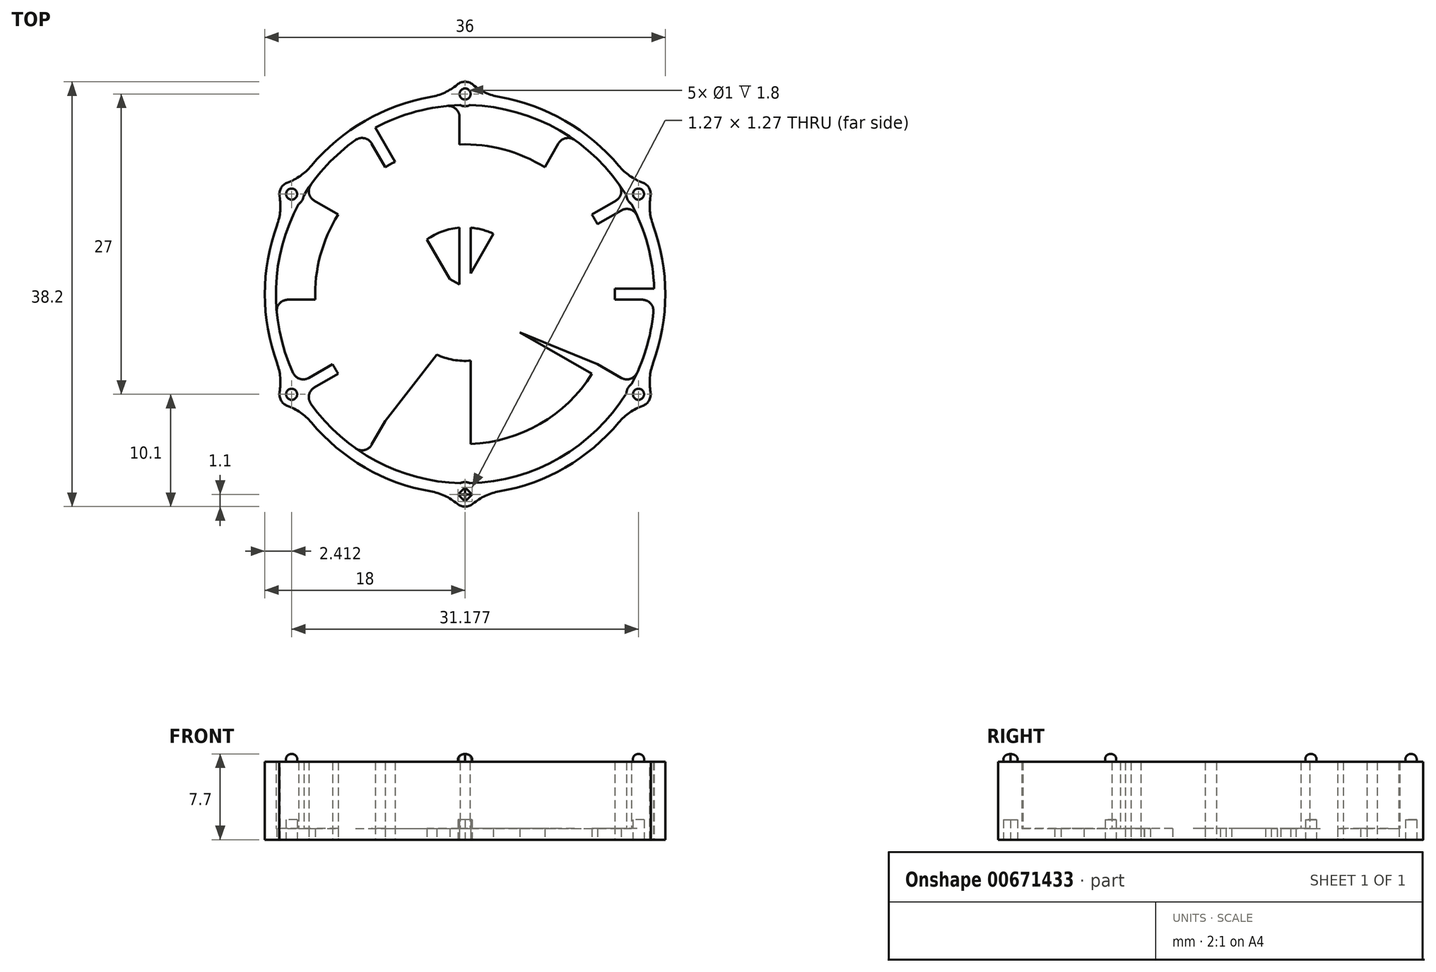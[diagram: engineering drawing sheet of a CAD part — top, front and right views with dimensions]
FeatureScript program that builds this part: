
annotation { "Feature Type Name" : "Feature", "Feature Type Description" : "" }
export const myFeature = defineFeature(function(context is Context, id is Id, definition is map)
    precondition{}
    {
        {
            var Q0;
            Q0=qCreatedBy(makeId("Top.planeOp"),FACE);
            var sketch = newSketch(context, id + "F0", { "sketchPlane" : qUnion([Q0])});
            skCircle(sketch, "E0", {"center": v(0, 0) * mm, "radius": 18 * mm});
            skCircle(sketch, "E1.0", {"center": v(0, 0) * mm, "radius": 17 * mm});
            skLineSegment(sketch, "E2.bottom", {"start": v(8.56, 15.83) * mm, "end": v(9.43, 15.33) * mm});
            skLineSegment(sketch, "E2.top", {"start": v(-9.43, -15.33) * mm, "end": v(-8.56, -15.83) * mm});
            skLineSegment(sketch, "E2.left", {"start": v(8.56, 15.83) * mm, "end": v(-9.43, -15.33) * mm});
            skLineSegment(sketch, "E2.right", {"start": v(9.43, 15.33) * mm, "end": v(-8.56, -15.83) * mm});
            skLineSegment(sketch, "E3.bottom", {"start": v(15.33, 9.43) * mm, "end": v(15.83, 8.56) * mm});
            skLineSegment(sketch, "E3.top", {"start": v(-15.83, -8.56) * mm, "end": v(-15.33, -9.43) * mm});
            skLineSegment(sketch, "E3.left", {"start": v(15.33, 9.43) * mm, "end": v(-15.83, -8.56) * mm});
            skLineSegment(sketch, "E3.right", {"start": v(15.83, 8.56) * mm, "end": v(-15.33, -9.43) * mm});
            skLineSegment(sketch, "E4", {"start": v(-38.35, 0) * mm, "end": v(39.17, 0) * mm, "construction": true});
            skLineSegment(sketch, "E5", {"start": v(0, 42.5) * mm, "end": v(0, -42.47) * mm, "construction": true});
            skLineSegment(sketch, "E6.bottom", {"start": v(-18, 0.5) * mm, "end": v(18, 0.5) * mm});
            skLineSegment(sketch, "E6.top", {"start": v(-18, -0.5) * mm, "end": v(18, -0.5) * mm});
            skLineSegment(sketch, "E6.left", {"start": v(-18, 0.5) * mm, "end": v(-18, -0.5) * mm});
            skLineSegment(sketch, "E6.right", {"start": v(18, 0.5) * mm, "end": v(18, -0.5) * mm});
            skLineSegment(sketch, "E7.bottom", {"start": v(-15.33, 9.43) * mm, "end": v(15.83, -8.56) * mm});
            skLineSegment(sketch, "E7.top", {"start": v(-15.83, 8.56) * mm, "end": v(15.33, -9.43) * mm});
            skLineSegment(sketch, "E7.left", {"start": v(-15.33, 9.43) * mm, "end": v(-15.83, 8.56) * mm});
            skLineSegment(sketch, "E7.right", {"start": v(15.83, -8.56) * mm, "end": v(15.33, -9.43) * mm});
            skLineSegment(sketch, "E8.bottom", {"start": v(-0.5, 18) * mm, "end": v(0.5, 18) * mm});
            skLineSegment(sketch, "E8.top", {"start": v(-0.5, -18) * mm, "end": v(0.5, -18) * mm});
            skLineSegment(sketch, "E8.left", {"start": v(-0.5, 18) * mm, "end": v(-0.5, -18) * mm});
            skLineSegment(sketch, "E8.right", {"start": v(0.5, 18) * mm, "end": v(0.5, -18) * mm});
            skLineSegment(sketch, "E9.bottom", {"start": v(-9.43, 15.33) * mm, "end": v(-8.56, 15.83) * mm});
            skLineSegment(sketch, "E9.top", {"start": v(8.56, -15.83) * mm, "end": v(9.43, -15.33) * mm});
            skLineSegment(sketch, "E9.left", {"start": v(-9.43, 15.33) * mm, "end": v(8.56, -15.83) * mm});
            skLineSegment(sketch, "E9.right", {"start": v(-8.56, 15.83) * mm, "end": v(9.43, -15.33) * mm});
            skCircle(sketch, "E10", {"center": v(0, 0) * mm, "radius": 13.47 * mm});
            skCircle(sketch, "E11", {"center": v(0, 0) * mm, "radius": 6 * mm});
            skLineSegment(sketch, "E12", {"start": v(-7.16, -11.4) * mm, "end": v(-2.56, -5.43) * mm});
            skLineSegment(sketch, "E13", {"start": v(4.93, -3.42) * mm, "end": v(11.9, -6.3) * mm});
            skSolve(sketch);
        }
        {
            var Q0;
            Q0=qCreatedBy(makeId("Top.planeOp"),FACE);
            var sketch = newSketch(context, id + "F1", { "sketchPlane" : qUnion([Q0])});
            skCircle(sketch, "E14", {"center": v(0, 0) * mm, "radius": 18 * mm});
            skCircle(sketch, "E15", {"center": v(0, 0) * mm, "radius": 17 * mm});
            skSolve(sketch);
        }
        {
            var Q0;
            Q0=makeQuery(id+"F1.imprint","IMPRINT",FACE,{"disambiguationData":[TD([[makeQuery(id+"F1.imprint","IMPRINT",EDGE,{"derivedFrom":sQuery(id+"F1.wireOp",EDGE,"E14")}),1.0]])]});
            extrude(context, id + "F2", {"entities" : qUnion([Q0]), "depth" : 7 * mm, "offsetDistance" : 25 * mm});
        }
        {
            var Q0;
            {var subQ0=sQuery(id+"F0.wireOp",EDGE,"E6.bottom");var subQ1=sQuery(id+"F0.wireOp",EDGE,"E1.0");var subQ2=makeQuery(id+"F0.imprint","INTERSECT",VERTEX,{"disambiguationData":[OD(0.0)],"derivedFrom":[subQ1,subQ0]});Q0=makeQuery(id+"F0.imprint","IMPRINT",FACE,{"disambiguationData":[TD([[makeQuery(id+"F0.imprint","IMPRINT",EDGE,{"disambiguationData":[TD([[subQ2,1.0]])],"derivedFrom":subQ1}),1.0]])]});}
            var Q1;
            {var subQ0=sQuery(id+"F0.wireOp",EDGE,"E3.left");var subQ1=sQuery(id+"F0.wireOp",EDGE,"E1.0");var subQ2=makeQuery(id+"F0.imprint","INTERSECT",VERTEX,{"disambiguationData":[OD(1.0)],"derivedFrom":[subQ1,subQ0]});Q1=makeQuery(id+"F0.imprint","IMPRINT",FACE,{"disambiguationData":[TD([[makeQuery(id+"F0.imprint","IMPRINT",EDGE,{"disambiguationData":[TD([[subQ2,-1.0]])],"derivedFrom":subQ1}),1.0]])]});}
            var Q2;
            {var subQ0=sQuery(id+"F0.wireOp",EDGE,"E9.right");var subQ1=sQuery(id+"F0.wireOp",EDGE,"E1.0");var subQ2=makeQuery(id+"F0.imprint","INTERSECT",VERTEX,{"disambiguationData":[OD(0.0)],"derivedFrom":[subQ1,subQ0]});Q2=makeQuery(id+"F0.imprint","IMPRINT",FACE,{"disambiguationData":[TD([[makeQuery(id+"F0.imprint","IMPRINT",EDGE,{"disambiguationData":[TD([[subQ2,-1.0]])],"derivedFrom":subQ1}),1.0]])]});}
            extrude(context, id + "F3", {"entities" : qUnion([Q0, Q1, Q2]), "operationType" : NewBodyOperationType.ADD, "depth" : 7 * mm, "offsetDistance" : 25 * mm});
        }
        {
            var Q0;
            Q0=makeQuery(id+"F1.imprint","IMPRINT",FACE,{"disambiguationData":[TD([[makeQuery(id+"F1.imprint","IMPRINT",EDGE,{"derivedFrom":sQuery(id+"F1.wireOp",EDGE,"E14")}),1.0]])]});
            var Q1;
            Q1=makeQuery(id+"F1.imprint","IMPRINT",FACE,{"disambiguationData":[TD([[makeQuery(id+"F1.imprint","IMPRINT",EDGE,{"derivedFrom":sQuery(id+"F1.wireOp",EDGE,"E15")}),1.0]])]});
            extrude(context, id + "F4", {"entities" : qUnion([Q0, Q1]), "operationType" : NewBodyOperationType.ADD, "depth" : 1 * mm, "offsetDistance" : 25 * mm});
        }
        {
            var Q0;
            Q0=qCreatedBy(makeId("Top.planeOp"),FACE);
            var sketch = newSketch(context, id + "F5", { "sketchPlane" : qUnion([Q0])});
            skCircle(sketch, "E16", {"center": v(0, 0) * mm, "radius": 18 * mm});
            skLineSegment(sketch, "E17", {"start": v(0, 18) * mm, "end": v(0, -18) * mm, "construction": true});
            skLineSegment(sketch, "E18", {"start": v(15.59, 9) * mm, "end": v(0, 0) * mm, "construction": true});
            skLineSegment(sketch, "E19", {"start": v(9, 15.59) * mm, "end": v(0, 0) * mm, "construction": true});
            skLineSegment(sketch, "E20", {"start": v(0, 0) * mm, "end": v(18, 0) * mm, "construction": true});
            skLineSegment(sketch, "E21", {"start": v(0, 0) * mm, "end": v(15.59, -9) * mm, "construction": true});
            skLineSegment(sketch, "E22", {"start": v(0, 0) * mm, "end": v(9, -15.59) * mm, "construction": true});
            skLineSegment(sketch, "E23", {"start": v(0, 0) * mm, "end": v(-9, 15.59) * mm, "construction": true});
            skLineSegment(sketch, "E24", {"start": v(0, 0) * mm, "end": v(-15.59, 9) * mm, "construction": true});
            skLineSegment(sketch, "E25", {"start": v(0, 0) * mm, "end": v(-18, 0) * mm, "construction": true});
            skLineSegment(sketch, "E26", {"start": v(0, 0) * mm, "end": v(-15.59, -9) * mm, "construction": true});
            skLineSegment(sketch, "E27", {"start": v(0, 0) * mm, "end": v(-9, -15.59) * mm, "construction": true});
            skCircle(sketch, "E28", {"center": v(0, 18) * mm, "radius": 1.1 * mm});
            skCircle(sketch, "E29", {"center": v(15.59, 9) * mm, "radius": 1.1 * mm});
            skCircle(sketch, "E30", {"center": v(15.59, -9) * mm, "radius": 1.1 * mm});
            skCircle(sketch, "E31", {"center": v(0, -18) * mm, "radius": 1.1 * mm});
            skCircle(sketch, "E32", {"center": v(-15.59, -9) * mm, "radius": 1.1 * mm});
            skCircle(sketch, "E33", {"center": v(-15.59, 9) * mm, "radius": 1.1 * mm});
            skCircle(sketch, "E34", {"center": v(-15.59, 9) * mm, "radius": 0.5 * mm});
            skCircle(sketch, "E35", {"center": v(0, 18) * mm, "radius": 0.5 * mm});
            skCircle(sketch, "E36", {"center": v(15.59, 9) * mm, "radius": 0.5 * mm});
            skCircle(sketch, "E37", {"center": v(15.59, -9) * mm, "radius": 0.5 * mm});
            skCircle(sketch, "E38", {"center": v(-15.59, -9) * mm, "radius": 0.5 * mm});
            skLineSegment(sketch, "E39.bottom", {"start": v(0.64, -18) * mm, "end": v(0, -18.64) * mm});
            skLineSegment(sketch, "E39.top", {"start": v(0, -17.36) * mm, "end": v(-0.64, -18) * mm});
            skLineSegment(sketch, "E39.left", {"start": v(0.64, -18) * mm, "end": v(0, -17.36) * mm});
            skLineSegment(sketch, "E39.right", {"start": v(0, -18.64) * mm, "end": v(-0.64, -18) * mm});
            skSolve(sketch);
        }
        {
            var Q0;
            {var subQ0=sQuery(id+"F5.wireOp",EDGE,"E33");var subQ1=sQuery(id+"F5.wireOp",EDGE,"E16");var subQ2=makeQuery(id+"F5.imprint","INTERSECT",VERTEX,{"disambiguationData":[OD(0.0)],"derivedFrom":[subQ1,subQ0]});Q0=makeQuery(id+"F5.imprint","IMPRINT",FACE,{"disambiguationData":[TD([[makeQuery(id+"F5.imprint","IMPRINT",EDGE,{"disambiguationData":[TD([[subQ2,-1.0]])],"derivedFrom":subQ1}),1.0]])]});}
            var Q1;
            {var subQ0=sQuery(id+"F5.wireOp",EDGE,"E33");var subQ1=sQuery(id+"F5.wireOp",EDGE,"E16");var subQ2=makeQuery(id+"F5.imprint","INTERSECT",VERTEX,{"disambiguationData":[OD(0.0)],"derivedFrom":[subQ1,subQ0]});Q1=makeQuery(id+"F5.imprint","IMPRINT",FACE,{"disambiguationData":[TD([[makeQuery(id+"F5.imprint","IMPRINT",EDGE,{"disambiguationData":[TD([[subQ2,-1.0]])],"derivedFrom":subQ1}),-1.0]])]});}
            var Q2;
            {var subQ0=sQuery(id+"F5.wireOp",EDGE,"E28");var subQ1=sQuery(id+"F5.wireOp",EDGE,"E16");var subQ2=makeQuery(id+"F5.imprint","INTERSECT",VERTEX,{"disambiguationData":[OD(0.0)],"derivedFrom":[subQ1,subQ0]});Q2=makeQuery(id+"F5.imprint","IMPRINT",FACE,{"disambiguationData":[TD([[makeQuery(id+"F5.imprint","IMPRINT",EDGE,{"disambiguationData":[TD([[subQ2,-1.0]])],"derivedFrom":subQ1}),1.0]])]});}
            var Q3;
            {var subQ0=sQuery(id+"F5.wireOp",EDGE,"E28");var subQ1=sQuery(id+"F5.wireOp",EDGE,"E16");var subQ2=makeQuery(id+"F5.imprint","INTERSECT",VERTEX,{"disambiguationData":[OD(0.0)],"derivedFrom":[subQ1,subQ0]});Q3=makeQuery(id+"F5.imprint","IMPRINT",FACE,{"disambiguationData":[TD([[makeQuery(id+"F5.imprint","IMPRINT",EDGE,{"disambiguationData":[TD([[subQ2,-1.0]])],"derivedFrom":subQ1}),-1.0]])]});}
            var Q4;
            {var subQ0=sQuery(id+"F5.wireOp",EDGE,"E29");var subQ1=sQuery(id+"F5.wireOp",EDGE,"E16");var subQ2=makeQuery(id+"F5.imprint","INTERSECT",VERTEX,{"disambiguationData":[OD(0.0)],"derivedFrom":[subQ1,subQ0]});Q4=makeQuery(id+"F5.imprint","IMPRINT",FACE,{"disambiguationData":[TD([[makeQuery(id+"F5.imprint","IMPRINT",EDGE,{"disambiguationData":[TD([[subQ2,-1.0]])],"derivedFrom":subQ1}),-1.0]])]});}
            var Q5;
            {var subQ0=sQuery(id+"F5.wireOp",EDGE,"E29");var subQ1=sQuery(id+"F5.wireOp",EDGE,"E16");var subQ2=makeQuery(id+"F5.imprint","INTERSECT",VERTEX,{"disambiguationData":[OD(0.0)],"derivedFrom":[subQ1,subQ0]});Q5=makeQuery(id+"F5.imprint","IMPRINT",FACE,{"disambiguationData":[TD([[makeQuery(id+"F5.imprint","IMPRINT",EDGE,{"disambiguationData":[TD([[subQ2,-1.0]])],"derivedFrom":subQ1}),1.0]])]});}
            var Q6;
            {var subQ0=sQuery(id+"F5.wireOp",EDGE,"E32");var subQ1=sQuery(id+"F5.wireOp",EDGE,"E16");var subQ2=makeQuery(id+"F5.imprint","INTERSECT",VERTEX,{"disambiguationData":[OD(0.0)],"derivedFrom":[subQ1,subQ0]});Q6=makeQuery(id+"F5.imprint","IMPRINT",FACE,{"disambiguationData":[TD([[makeQuery(id+"F5.imprint","IMPRINT",EDGE,{"disambiguationData":[TD([[subQ2,-1.0]])],"derivedFrom":subQ1}),1.0]])]});}
            var Q7;
            {var subQ0=sQuery(id+"F5.wireOp",EDGE,"E32");var subQ1=sQuery(id+"F5.wireOp",EDGE,"E16");var subQ2=makeQuery(id+"F5.imprint","INTERSECT",VERTEX,{"disambiguationData":[OD(0.0)],"derivedFrom":[subQ1,subQ0]});Q7=makeQuery(id+"F5.imprint","IMPRINT",FACE,{"disambiguationData":[TD([[makeQuery(id+"F5.imprint","IMPRINT",EDGE,{"disambiguationData":[TD([[subQ2,-1.0]])],"derivedFrom":subQ1}),-1.0]])]});}
            var Q8;
            {var subQ3=sQuery(id+"F5.wireOp",EDGE,"E16");var subQ5=sQuery(id+"F5.wireOp",EDGE,"E31");var subQ6=makeQuery(id+"F5.imprint","INTERSECT",VERTEX,{"disambiguationData":[OD(0.0)],"derivedFrom":[subQ3,subQ5]});Q8=makeQuery(id+"F5.imprint","IMPRINT",FACE,{"disambiguationData":[TD([[makeQuery(id+"F5.imprint","IMPRINT",EDGE,{"disambiguationData":[TD([[subQ6,-1.0]])],"derivedFrom":subQ3}),1.0]])]});}
            var Q9;
            {var subQ6=sQuery(id+"F5.wireOp",EDGE,"E39.bottom");Q9=makeQuery(id+"F5.imprint","IMPRINT",FACE,{"disambiguationData":[TD([[makeQuery(id+"F5.imprint","IMPRINT",EDGE,{"derivedFrom":subQ6}),1.0]])]});}
            var Q10;
            {var subQ0=sQuery(id+"F5.wireOp",EDGE,"E30");var subQ1=sQuery(id+"F5.wireOp",EDGE,"E16");var subQ2=makeQuery(id+"F5.imprint","INTERSECT",VERTEX,{"disambiguationData":[OD(0.0)],"derivedFrom":[subQ1,subQ0]});Q10=makeQuery(id+"F5.imprint","IMPRINT",FACE,{"disambiguationData":[TD([[makeQuery(id+"F5.imprint","IMPRINT",EDGE,{"disambiguationData":[TD([[subQ2,-1.0]])],"derivedFrom":subQ1}),-1.0]])]});}
            var Q11;
            {var subQ0=sQuery(id+"F5.wireOp",EDGE,"E30");var subQ1=sQuery(id+"F5.wireOp",EDGE,"E16");var subQ2=makeQuery(id+"F5.imprint","INTERSECT",VERTEX,{"disambiguationData":[OD(0.0)],"derivedFrom":[subQ1,subQ0]});Q11=makeQuery(id+"F5.imprint","IMPRINT",FACE,{"disambiguationData":[TD([[makeQuery(id+"F5.imprint","IMPRINT",EDGE,{"disambiguationData":[TD([[subQ2,-1.0]])],"derivedFrom":subQ1}),1.0]])]});}
            var Q12;
            {var subQ0=sQuery(id+"F5.wireOp",EDGE,"E34");var subQ1=sQuery(id+"F5.wireOp",EDGE,"E16");var subQ2=makeQuery(id+"F5.imprint","INTERSECT",VERTEX,{"disambiguationData":[OD(0.0)],"derivedFrom":[subQ1,subQ0]});Q12=makeQuery(id+"F5.imprint","IMPRINT",FACE,{"disambiguationData":[TD([[makeQuery(id+"F5.imprint","IMPRINT",EDGE,{"disambiguationData":[TD([[subQ2,-1.0]])],"derivedFrom":subQ1}),1.0]])]});}
            var Q13;
            {var subQ0=sQuery(id+"F5.wireOp",EDGE,"E34");var subQ1=sQuery(id+"F5.wireOp",EDGE,"E16");var subQ2=makeQuery(id+"F5.imprint","INTERSECT",VERTEX,{"disambiguationData":[OD(0.0)],"derivedFrom":[subQ1,subQ0]});Q13=makeQuery(id+"F5.imprint","IMPRINT",FACE,{"disambiguationData":[TD([[makeQuery(id+"F5.imprint","IMPRINT",EDGE,{"disambiguationData":[TD([[subQ2,-1.0]])],"derivedFrom":subQ1}),-1.0]])]});}
            var Q14;
            {var subQ0=sQuery(id+"F5.wireOp",EDGE,"E35");var subQ1=sQuery(id+"F5.wireOp",EDGE,"E16");var subQ2=makeQuery(id+"F5.imprint","INTERSECT",VERTEX,{"disambiguationData":[OD(0.0)],"derivedFrom":[subQ1,subQ0]});Q14=makeQuery(id+"F5.imprint","IMPRINT",FACE,{"disambiguationData":[TD([[makeQuery(id+"F5.imprint","IMPRINT",EDGE,{"disambiguationData":[TD([[subQ2,-1.0]])],"derivedFrom":subQ1}),-1.0]])]});}
            var Q15;
            {var subQ0=sQuery(id+"F5.wireOp",EDGE,"E35");var subQ1=sQuery(id+"F5.wireOp",EDGE,"E16");var subQ2=makeQuery(id+"F5.imprint","INTERSECT",VERTEX,{"disambiguationData":[OD(0.0)],"derivedFrom":[subQ1,subQ0]});Q15=makeQuery(id+"F5.imprint","IMPRINT",FACE,{"disambiguationData":[TD([[makeQuery(id+"F5.imprint","IMPRINT",EDGE,{"disambiguationData":[TD([[subQ2,-1.0]])],"derivedFrom":subQ1}),1.0]])]});}
            var Q16;
            {var subQ0=sQuery(id+"F5.wireOp",EDGE,"E36");var subQ1=sQuery(id+"F5.wireOp",EDGE,"E16");var subQ2=makeQuery(id+"F5.imprint","INTERSECT",VERTEX,{"disambiguationData":[OD(0.0)],"derivedFrom":[subQ1,subQ0]});Q16=makeQuery(id+"F5.imprint","IMPRINT",FACE,{"disambiguationData":[TD([[makeQuery(id+"F5.imprint","IMPRINT",EDGE,{"disambiguationData":[TD([[subQ2,-1.0]])],"derivedFrom":subQ1}),-1.0]])]});}
            var Q17;
            {var subQ0=sQuery(id+"F5.wireOp",EDGE,"E36");var subQ1=sQuery(id+"F5.wireOp",EDGE,"E16");var subQ2=makeQuery(id+"F5.imprint","INTERSECT",VERTEX,{"disambiguationData":[OD(0.0)],"derivedFrom":[subQ1,subQ0]});Q17=makeQuery(id+"F5.imprint","IMPRINT",FACE,{"disambiguationData":[TD([[makeQuery(id+"F5.imprint","IMPRINT",EDGE,{"disambiguationData":[TD([[subQ2,-1.0]])],"derivedFrom":subQ1}),1.0]])]});}
            var Q18;
            {var subQ0=sQuery(id+"F5.wireOp",EDGE,"E37");var subQ1=sQuery(id+"F5.wireOp",EDGE,"E16");var subQ2=makeQuery(id+"F5.imprint","INTERSECT",VERTEX,{"disambiguationData":[OD(0.0)],"derivedFrom":[subQ1,subQ0]});Q18=makeQuery(id+"F5.imprint","IMPRINT",FACE,{"disambiguationData":[TD([[makeQuery(id+"F5.imprint","IMPRINT",EDGE,{"disambiguationData":[TD([[subQ2,-1.0]])],"derivedFrom":subQ1}),-1.0]])]});}
            var Q19;
            {var subQ0=sQuery(id+"F5.wireOp",EDGE,"E37");var subQ1=sQuery(id+"F5.wireOp",EDGE,"E16");var subQ2=makeQuery(id+"F5.imprint","INTERSECT",VERTEX,{"disambiguationData":[OD(0.0)],"derivedFrom":[subQ1,subQ0]});Q19=makeQuery(id+"F5.imprint","IMPRINT",FACE,{"disambiguationData":[TD([[makeQuery(id+"F5.imprint","IMPRINT",EDGE,{"disambiguationData":[TD([[subQ2,-1.0]])],"derivedFrom":subQ1}),1.0]])]});}
            var Q20;
            {var subQ1=sQuery(id+"F5.wireOp",EDGE,"E39.bottom");Q20=makeQuery(id+"F5.imprint","IMPRINT",FACE,{"disambiguationData":[TD([[makeQuery(id+"F5.imprint","IMPRINT",EDGE,{"derivedFrom":subQ1}),-1.0]])]});}
            var Q21;
            {var subQ0=sQuery(id+"F5.wireOp",EDGE,"E38");var subQ1=sQuery(id+"F5.wireOp",EDGE,"E16");var subQ2=makeQuery(id+"F5.imprint","INTERSECT",VERTEX,{"disambiguationData":[OD(0.0)],"derivedFrom":[subQ1,subQ0]});Q21=makeQuery(id+"F5.imprint","IMPRINT",FACE,{"disambiguationData":[TD([[makeQuery(id+"F5.imprint","IMPRINT",EDGE,{"disambiguationData":[TD([[subQ2,-1.0]])],"derivedFrom":subQ1}),-1.0]])]});}
            var Q22;
            {var subQ0=sQuery(id+"F5.wireOp",EDGE,"E38");var subQ1=sQuery(id+"F5.wireOp",EDGE,"E16");var subQ2=makeQuery(id+"F5.imprint","INTERSECT",VERTEX,{"disambiguationData":[OD(0.0)],"derivedFrom":[subQ1,subQ0]});Q22=makeQuery(id+"F5.imprint","IMPRINT",FACE,{"disambiguationData":[TD([[makeQuery(id+"F5.imprint","IMPRINT",EDGE,{"disambiguationData":[TD([[subQ2,-1.0]])],"derivedFrom":subQ1}),1.0]])]});}
            var Q23;
            {var subQ0=sQuery(id+"F5.wireOp",EDGE,"E39.top");var subQ1=sQuery(id+"F5.wireOp",EDGE,"E16");var subQ2=makeQuery(id+"F5.imprint","INTERSECT",VERTEX,{"derivedFrom":[subQ1,subQ0]});Q23=makeQuery(id+"F5.imprint","IMPRINT",FACE,{"disambiguationData":[TD([[makeQuery(id+"F5.imprint","IMPRINT",EDGE,{"disambiguationData":[TD([[subQ2,-1.0]])],"derivedFrom":subQ1}),1.0]])]});}
            extrude(context, id + "F6", {"entities" : qUnion([Q0, Q1, Q2, Q3, Q4, Q5, Q6, Q7, Q8, Q9, Q10, Q11, Q12, Q13, Q14, Q15, Q16, Q17, Q18, Q19, Q20, Q21, Q22, Q23]), "operationType" : NewBodyOperationType.ADD, "depth" : 7 * mm, "offsetDistance" : 25 * mm});
        }
        {
            var Q0;
            {var subQ0=sQuery(id+"F0.wireOp",EDGE,"E8.right");var subQ1=sQuery(id+"F0.wireOp",EDGE,"E1.0");Q0=makeQuery(id+"F3.opExtrude","SWEPT_EDGE",EDGE,{"disambiguationData":[OSD([subQ1,subQ0]),TDD([makeQuery(id+"F0.imprint","INTERSECT",VERTEX,{"disambiguationData":[OD(1.0)],"derivedFrom":[subQ1,subQ0]})])]});}
            var Q1;
            {var subQ0=sQuery(id+"F0.wireOp",EDGE,"E2.left");var subQ1=sQuery(id+"F0.wireOp",EDGE,"E1.0");Q1=makeQuery(id+"F3.opExtrude","SWEPT_EDGE",EDGE,{"disambiguationData":[OSD([subQ1,subQ0]),TDD([makeQuery(id+"F0.imprint","INTERSECT",VERTEX,{"disambiguationData":[OD(1.0)],"derivedFrom":[subQ1,subQ0]})])]});}
            var Q2;
            {var subQ0=sQuery(id+"F0.wireOp",EDGE,"E3.left");var subQ1=sQuery(id+"F0.wireOp",EDGE,"E1.0");Q2=makeQuery(id+"F3.opExtrude","SWEPT_EDGE",EDGE,{"disambiguationData":[OSD([subQ1,subQ0]),TDD([makeQuery(id+"F0.imprint","INTERSECT",VERTEX,{"disambiguationData":[OD(1.0)],"derivedFrom":[subQ1,subQ0]})])]});}
            var Q3;
            {var subQ0=sQuery(id+"F0.wireOp",EDGE,"E6.bottom");var subQ1=sQuery(id+"F0.wireOp",EDGE,"E1.0");Q3=makeQuery(id+"F3.opExtrude","SWEPT_EDGE",EDGE,{"disambiguationData":[OSD([subQ1,subQ0]),TDD([makeQuery(id+"F0.imprint","INTERSECT",VERTEX,{"disambiguationData":[OD(1.0)],"derivedFrom":[subQ1,subQ0]})])]});}
            var Q4;
            {var subQ0=sQuery(id+"F0.wireOp",EDGE,"E9.right");var subQ1=sQuery(id+"F0.wireOp",EDGE,"E1.0");Q4=makeQuery(id+"F3.opExtrude","SWEPT_EDGE",EDGE,{"disambiguationData":[OSD([subQ1,subQ0]),TDD([makeQuery(id+"F0.imprint","INTERSECT",VERTEX,{"disambiguationData":[OD(1.0)],"derivedFrom":[subQ1,subQ0]})])]});}
            var Q5;
            {var subQ0=sQuery(id+"F0.wireOp",EDGE,"E7.bottom");var subQ1=sQuery(id+"F0.wireOp",EDGE,"E1.0");Q5=makeQuery(id+"F3.opExtrude","SWEPT_EDGE",EDGE,{"disambiguationData":[OSD([subQ1,subQ0]),TDD([makeQuery(id+"F0.imprint","INTERSECT",VERTEX,{"disambiguationData":[OD(1.0)],"derivedFrom":[subQ1,subQ0]})])]});}
            var Q6;
            {var subQ0=sQuery(id+"F0.wireOp",EDGE,"E8.left");var subQ1=sQuery(id+"F0.wireOp",EDGE,"E1.0");Q6=makeQuery(id+"F3.opExtrude","SWEPT_EDGE",EDGE,{"disambiguationData":[OSD([subQ1,subQ0]),TDD([makeQuery(id+"F0.imprint","INTERSECT",VERTEX,{"disambiguationData":[OD(0.0)],"derivedFrom":[subQ1,subQ0]})])]});}
            var Q7;
            {var subQ0=sQuery(id+"F0.wireOp",EDGE,"E2.left");var subQ1=sQuery(id+"F0.wireOp",EDGE,"E1.0");Q7=makeQuery(id+"F3.opExtrude","SWEPT_EDGE",EDGE,{"disambiguationData":[OSD([subQ1,subQ0]),TDD([makeQuery(id+"F0.imprint","INTERSECT",VERTEX,{"disambiguationData":[OD(0.0)],"derivedFrom":[subQ1,subQ0]})])]});}
            var Q8;
            {var subQ0=sQuery(id+"F0.wireOp",EDGE,"E3.left");var subQ1=sQuery(id+"F0.wireOp",EDGE,"E1.0");Q8=makeQuery(id+"F3.opExtrude","SWEPT_EDGE",EDGE,{"disambiguationData":[OSD([subQ1,subQ0]),TDD([makeQuery(id+"F0.imprint","INTERSECT",VERTEX,{"disambiguationData":[OD(0.0)],"derivedFrom":[subQ1,subQ0]})])]});}
            var Q9;
            {var subQ0=sQuery(id+"F0.wireOp",EDGE,"E6.top");var subQ1=sQuery(id+"F0.wireOp",EDGE,"E1.0");Q9=makeQuery(id+"F3.opExtrude","SWEPT_EDGE",EDGE,{"disambiguationData":[OSD([subQ1,subQ0]),TDD([makeQuery(id+"F0.imprint","INTERSECT",VERTEX,{"disambiguationData":[OD(1.0)],"derivedFrom":[subQ1,subQ0]})])]});}
            var Q10;
            {var subQ0=sQuery(id+"F0.wireOp",EDGE,"E7.top");var subQ1=sQuery(id+"F0.wireOp",EDGE,"E1.0");Q10=makeQuery(id+"F3.opExtrude","SWEPT_EDGE",EDGE,{"disambiguationData":[OSD([subQ1,subQ0]),TDD([makeQuery(id+"F0.imprint","INTERSECT",VERTEX,{"disambiguationData":[OD(0.0)],"derivedFrom":[subQ1,subQ0]})])]});}
            var Q11;
            {var subQ0=sQuery(id+"F0.wireOp",EDGE,"E6.top");var subQ1=sQuery(id+"F0.wireOp",EDGE,"E1.0");Q11=makeQuery(id+"F3.opExtrude","SWEPT_EDGE",EDGE,{"disambiguationData":[OSD([subQ1,subQ0]),TDD([makeQuery(id+"F0.imprint","INTERSECT",VERTEX,{"disambiguationData":[OD(0.0)],"derivedFrom":[subQ1,subQ0]})])]});}
            var Q12;
            {var subQ0=sQuery(id+"F0.wireOp",EDGE,"E9.left");var subQ1=sQuery(id+"F0.wireOp",EDGE,"E1.0");Q12=makeQuery(id+"F3.opExtrude","SWEPT_EDGE",EDGE,{"disambiguationData":[OSD([subQ1,subQ0]),TDD([makeQuery(id+"F0.imprint","INTERSECT",VERTEX,{"disambiguationData":[OD(0.0)],"derivedFrom":[subQ1,subQ0]})])]});}
            var Q13;
            {var subQ0=sQuery(id+"F0.wireOp",EDGE,"E8.right");var subQ1=sQuery(id+"F0.wireOp",EDGE,"E1.0");Q13=makeQuery(id+"F3.opExtrude","SWEPT_EDGE",EDGE,{"disambiguationData":[OSD([subQ1,subQ0]),TDD([makeQuery(id+"F0.imprint","INTERSECT",VERTEX,{"disambiguationData":[OD(0.0)],"derivedFrom":[subQ1,subQ0]})])]});}
            var Q14;
            {var subQ0=sQuery(id+"F0.wireOp",EDGE,"E7.bottom");var subQ1=sQuery(id+"F0.wireOp",EDGE,"E1.0");Q14=makeQuery(id+"F3.opExtrude","SWEPT_EDGE",EDGE,{"disambiguationData":[OSD([subQ1,subQ0]),TDD([makeQuery(id+"F0.imprint","INTERSECT",VERTEX,{"disambiguationData":[OD(0.0)],"derivedFrom":[subQ1,subQ0]})])]});}
            var Q15;
            {var subQ0=sQuery(id+"F0.wireOp",EDGE,"E9.right");var subQ1=sQuery(id+"F0.wireOp",EDGE,"E1.0");Q15=makeQuery(id+"F3.opExtrude","SWEPT_EDGE",EDGE,{"disambiguationData":[OSD([subQ1,subQ0]),TDD([makeQuery(id+"F0.imprint","INTERSECT",VERTEX,{"disambiguationData":[OD(0.0)],"derivedFrom":[subQ1,subQ0]})])]});}
            var Q16;
            {var subQ0=sQuery(id+"F0.wireOp",EDGE,"E3.right");var subQ1=sQuery(id+"F0.wireOp",EDGE,"E1.0");Q16=makeQuery(id+"F3.opExtrude","SWEPT_EDGE",EDGE,{"disambiguationData":[OSD([subQ1,subQ0]),TDD([makeQuery(id+"F0.imprint","INTERSECT",VERTEX,{"disambiguationData":[OD(1.0)],"derivedFrom":[subQ1,subQ0]})])]});}
            var Q17;
            {var subQ0=sQuery(id+"F0.wireOp",EDGE,"E2.right");var subQ1=sQuery(id+"F0.wireOp",EDGE,"E1.0");Q17=makeQuery(id+"F3.opExtrude","SWEPT_EDGE",EDGE,{"disambiguationData":[OSD([subQ1,subQ0]),TDD([makeQuery(id+"F0.imprint","INTERSECT",VERTEX,{"disambiguationData":[OD(1.0)],"derivedFrom":[subQ1,subQ0]})])]});}
            var Q18;
            {var subQ0=sQuery(id+"F0.wireOp",EDGE,"E3.right");var subQ1=sQuery(id+"F0.wireOp",EDGE,"E1.0");Q18=makeQuery(id+"F3.opExtrude","SWEPT_EDGE",EDGE,{"disambiguationData":[OSD([subQ1,subQ0]),TDD([makeQuery(id+"F0.imprint","INTERSECT",VERTEX,{"disambiguationData":[OD(0.0)],"derivedFrom":[subQ1,subQ0]})])]});}
            var Q19;
            {var subQ0=sQuery(id+"F0.wireOp",EDGE,"E2.right");var subQ1=sQuery(id+"F0.wireOp",EDGE,"E1.0");Q19=makeQuery(id+"F3.opExtrude","SWEPT_EDGE",EDGE,{"disambiguationData":[OSD([subQ1,subQ0]),TDD([makeQuery(id+"F0.imprint","INTERSECT",VERTEX,{"disambiguationData":[OD(0.0)],"derivedFrom":[subQ1,subQ0]})])]});}
            var Q20;
            {var subQ0=sQuery(id+"F0.wireOp",EDGE,"E8.left");var subQ1=sQuery(id+"F0.wireOp",EDGE,"E1.0");Q20=makeQuery(id+"F3.opExtrude","SWEPT_EDGE",EDGE,{"disambiguationData":[OSD([subQ1,subQ0]),TDD([makeQuery(id+"F0.imprint","INTERSECT",VERTEX,{"disambiguationData":[OD(1.0)],"derivedFrom":[subQ1,subQ0]})])]});}
            var Q21;
            {var subQ0=sQuery(id+"F0.wireOp",EDGE,"E9.left");var subQ1=sQuery(id+"F0.wireOp",EDGE,"E1.0");Q21=makeQuery(id+"F3.opExtrude","SWEPT_EDGE",EDGE,{"disambiguationData":[OSD([subQ1,subQ0]),TDD([makeQuery(id+"F0.imprint","INTERSECT",VERTEX,{"disambiguationData":[OD(1.0)],"derivedFrom":[subQ1,subQ0]})])]});}
            var Q22;
            {var subQ0=sQuery(id+"F0.wireOp",EDGE,"E7.top");var subQ1=sQuery(id+"F0.wireOp",EDGE,"E1.0");Q22=makeQuery(id+"F3.opExtrude","SWEPT_EDGE",EDGE,{"disambiguationData":[OSD([subQ1,subQ0]),TDD([makeQuery(id+"F0.imprint","INTERSECT",VERTEX,{"disambiguationData":[OD(1.0)],"derivedFrom":[subQ1,subQ0]})])]});}
            var Q23;
            {var subQ0=sQuery(id+"F0.wireOp",EDGE,"E6.bottom");var subQ1=sQuery(id+"F0.wireOp",EDGE,"E1.0");Q23=makeQuery(id+"F3.opExtrude","SWEPT_EDGE",EDGE,{"disambiguationData":[OSD([subQ1,subQ0]),TDD([makeQuery(id+"F0.imprint","INTERSECT",VERTEX,{"disambiguationData":[OD(0.0)],"derivedFrom":[subQ1,subQ0]})])]});}
            fillet(context, id + "F7", {"entities" : qUnion([Q0, Q1, Q2, Q3, Q4, Q5, Q6, Q7, Q8, Q9, Q10, Q11, Q12, Q13, Q14, Q15, Q16, Q17, Q18, Q19, Q20, Q21, Q22, Q23]), "radius" : 1 * mm, "tangentPropagation" : true, "allowEdgeOverflow" : false});
        }
        {
            var Q0;
            Q0=makeQuery(id+"F6.boolean.opBoolean","INTERSECT",EDGE,{"disambiguationData":[OD(0.0)],"derivedFrom":[makeQuery(id+"F2.opExtrude","SWEPT_FACE",FACE,{"disambiguationData":[OSD([sQuery(id+"F1.wireOp",EDGE,"E14")])]}),makeQuery(id+"F6.opExtrude","SWEPT_FACE",FACE,{"disambiguationData":[OSD([sQuery(id+"F5.wireOp",EDGE,"E33")])]})]});
            var Q1;
            Q1=makeQuery(id+"F6.boolean.opBoolean","INTERSECT",EDGE,{"disambiguationData":[OD(1.0)],"derivedFrom":[makeQuery(id+"F2.opExtrude","SWEPT_FACE",FACE,{"disambiguationData":[OSD([sQuery(id+"F1.wireOp",EDGE,"E14")])]}),makeQuery(id+"F6.opExtrude","SWEPT_FACE",FACE,{"disambiguationData":[OSD([sQuery(id+"F5.wireOp",EDGE,"E33")])]})]});
            var Q2;
            Q2=makeQuery(id+"F6.boolean.opBoolean","INTERSECT",EDGE,{"disambiguationData":[OD(1.0)],"derivedFrom":[makeQuery(id+"F2.opExtrude","SWEPT_FACE",FACE,{"disambiguationData":[OSD([sQuery(id+"F1.wireOp",EDGE,"E14")])]}),makeQuery(id+"F6.opExtrude","SWEPT_FACE",FACE,{"disambiguationData":[OSD([sQuery(id+"F5.wireOp",EDGE,"E28")])]})]});
            var Q3;
            Q3=makeQuery(id+"F6.boolean.opBoolean","INTERSECT",EDGE,{"disambiguationData":[OD(1.0)],"derivedFrom":[makeQuery(id+"F2.opExtrude","SWEPT_FACE",FACE,{"disambiguationData":[OSD([sQuery(id+"F1.wireOp",EDGE,"E14")])]}),makeQuery(id+"F6.opExtrude","SWEPT_FACE",FACE,{"disambiguationData":[OSD([sQuery(id+"F5.wireOp",EDGE,"E32")])]})]});
            var Q4;
            Q4=makeQuery(id+"F6.boolean.opBoolean","INTERSECT",EDGE,{"disambiguationData":[OD(0.0)],"derivedFrom":[makeQuery(id+"F2.opExtrude","SWEPT_FACE",FACE,{"disambiguationData":[OSD([sQuery(id+"F1.wireOp",EDGE,"E14")])]}),makeQuery(id+"F6.opExtrude","SWEPT_FACE",FACE,{"disambiguationData":[OSD([sQuery(id+"F5.wireOp",EDGE,"E32")])]})]});
            var Q5;
            Q5=makeQuery(id+"F6.boolean.opBoolean","INTERSECT",EDGE,{"disambiguationData":[OD(1.0)],"derivedFrom":[makeQuery(id+"F2.opExtrude","SWEPT_FACE",FACE,{"disambiguationData":[OSD([sQuery(id+"F1.wireOp",EDGE,"E14")])]}),makeQuery(id+"F6.opExtrude","SWEPT_FACE",FACE,{"disambiguationData":[OSD([sQuery(id+"F5.wireOp",EDGE,"E31")])]})]});
            var Q6;
            Q6=makeQuery(id+"F6.boolean.opBoolean","INTERSECT",EDGE,{"disambiguationData":[OD(0.0)],"derivedFrom":[makeQuery(id+"F2.opExtrude","SWEPT_FACE",FACE,{"disambiguationData":[OSD([sQuery(id+"F1.wireOp",EDGE,"E14")])]}),makeQuery(id+"F6.opExtrude","SWEPT_FACE",FACE,{"disambiguationData":[OSD([sQuery(id+"F5.wireOp",EDGE,"E31")])]})]});
            var Q7;
            Q7=makeQuery(id+"F6.boolean.opBoolean","INTERSECT",EDGE,{"disambiguationData":[OD(1.0)],"derivedFrom":[makeQuery(id+"F2.opExtrude","SWEPT_FACE",FACE,{"disambiguationData":[OSD([sQuery(id+"F1.wireOp",EDGE,"E14")])]}),makeQuery(id+"F6.opExtrude","SWEPT_FACE",FACE,{"disambiguationData":[OSD([sQuery(id+"F5.wireOp",EDGE,"E30")])]})]});
            var Q8;
            Q8=makeQuery(id+"F6.boolean.opBoolean","INTERSECT",EDGE,{"disambiguationData":[OD(0.0)],"derivedFrom":[makeQuery(id+"F2.opExtrude","SWEPT_FACE",FACE,{"disambiguationData":[OSD([sQuery(id+"F1.wireOp",EDGE,"E14")])]}),makeQuery(id+"F6.opExtrude","SWEPT_FACE",FACE,{"disambiguationData":[OSD([sQuery(id+"F5.wireOp",EDGE,"E30")])]})]});
            var Q9;
            Q9=makeQuery(id+"F6.boolean.opBoolean","INTERSECT",EDGE,{"disambiguationData":[OD(1.0)],"derivedFrom":[makeQuery(id+"F2.opExtrude","SWEPT_FACE",FACE,{"disambiguationData":[OSD([sQuery(id+"F1.wireOp",EDGE,"E14")])]}),makeQuery(id+"F6.opExtrude","SWEPT_FACE",FACE,{"disambiguationData":[OSD([sQuery(id+"F5.wireOp",EDGE,"E29")])]})]});
            var Q10;
            Q10=makeQuery(id+"F6.boolean.opBoolean","INTERSECT",EDGE,{"disambiguationData":[OD(0.0)],"derivedFrom":[makeQuery(id+"F2.opExtrude","SWEPT_FACE",FACE,{"disambiguationData":[OSD([sQuery(id+"F1.wireOp",EDGE,"E14")])]}),makeQuery(id+"F6.opExtrude","SWEPT_FACE",FACE,{"disambiguationData":[OSD([sQuery(id+"F5.wireOp",EDGE,"E29")])]})]});
            var Q11;
            Q11=makeQuery(id+"F6.boolean.opBoolean","INTERSECT",EDGE,{"disambiguationData":[OD(0.0)],"derivedFrom":[makeQuery(id+"F2.opExtrude","SWEPT_FACE",FACE,{"disambiguationData":[OSD([sQuery(id+"F1.wireOp",EDGE,"E14")])]}),makeQuery(id+"F6.opExtrude","SWEPT_FACE",FACE,{"disambiguationData":[OSD([sQuery(id+"F5.wireOp",EDGE,"E28")])]})]});
            fillet(context, id + "F8", {"entities" : qUnion([Q0, Q1, Q2, Q3, Q4, Q5, Q6, Q7, Q8, Q9, Q10, Q11]), "radius" : 5 * mm, "tangentPropagation" : true, "allowEdgeOverflow" : false});
        }
        {
            var Q0;
            {var subQ0=sQuery(id+"F5.wireOp",EDGE,"E34");var subQ1=sQuery(id+"F5.wireOp",EDGE,"E16");var subQ2=makeQuery(id+"F5.imprint","INTERSECT",VERTEX,{"disambiguationData":[OD(0.0)],"derivedFrom":[subQ1,subQ0]});Q0=makeQuery(id+"F5.imprint","IMPRINT",FACE,{"disambiguationData":[TD([[makeQuery(id+"F5.imprint","IMPRINT",EDGE,{"disambiguationData":[TD([[subQ2,-1.0]])],"derivedFrom":subQ1}),-1.0]])]});}
            var Q1;
            {var subQ0=sQuery(id+"F5.wireOp",EDGE,"E34");var subQ1=sQuery(id+"F5.wireOp",EDGE,"E16");var subQ2=makeQuery(id+"F5.imprint","INTERSECT",VERTEX,{"disambiguationData":[OD(0.0)],"derivedFrom":[subQ1,subQ0]});Q1=makeQuery(id+"F5.imprint","IMPRINT",FACE,{"disambiguationData":[TD([[makeQuery(id+"F5.imprint","IMPRINT",EDGE,{"disambiguationData":[TD([[subQ2,-1.0]])],"derivedFrom":subQ1}),1.0]])]});}
            var Q2;
            {var subQ0=sQuery(id+"F5.wireOp",EDGE,"E35");var subQ1=sQuery(id+"F5.wireOp",EDGE,"E16");var subQ2=makeQuery(id+"F5.imprint","INTERSECT",VERTEX,{"disambiguationData":[OD(0.0)],"derivedFrom":[subQ1,subQ0]});Q2=makeQuery(id+"F5.imprint","IMPRINT",FACE,{"disambiguationData":[TD([[makeQuery(id+"F5.imprint","IMPRINT",EDGE,{"disambiguationData":[TD([[subQ2,-1.0]])],"derivedFrom":subQ1}),-1.0]])]});}
            var Q3;
            {var subQ0=sQuery(id+"F5.wireOp",EDGE,"E35");var subQ1=sQuery(id+"F5.wireOp",EDGE,"E16");var subQ2=makeQuery(id+"F5.imprint","INTERSECT",VERTEX,{"disambiguationData":[OD(0.0)],"derivedFrom":[subQ1,subQ0]});Q3=makeQuery(id+"F5.imprint","IMPRINT",FACE,{"disambiguationData":[TD([[makeQuery(id+"F5.imprint","IMPRINT",EDGE,{"disambiguationData":[TD([[subQ2,-1.0]])],"derivedFrom":subQ1}),1.0]])]});}
            var Q4;
            {var subQ0=sQuery(id+"F5.wireOp",EDGE,"E36");var subQ1=sQuery(id+"F5.wireOp",EDGE,"E16");var subQ2=makeQuery(id+"F5.imprint","INTERSECT",VERTEX,{"disambiguationData":[OD(0.0)],"derivedFrom":[subQ1,subQ0]});Q4=makeQuery(id+"F5.imprint","IMPRINT",FACE,{"disambiguationData":[TD([[makeQuery(id+"F5.imprint","IMPRINT",EDGE,{"disambiguationData":[TD([[subQ2,-1.0]])],"derivedFrom":subQ1}),1.0]])]});}
            var Q5;
            {var subQ0=sQuery(id+"F5.wireOp",EDGE,"E36");var subQ1=sQuery(id+"F5.wireOp",EDGE,"E16");var subQ2=makeQuery(id+"F5.imprint","INTERSECT",VERTEX,{"disambiguationData":[OD(0.0)],"derivedFrom":[subQ1,subQ0]});Q5=makeQuery(id+"F5.imprint","IMPRINT",FACE,{"disambiguationData":[TD([[makeQuery(id+"F5.imprint","IMPRINT",EDGE,{"disambiguationData":[TD([[subQ2,-1.0]])],"derivedFrom":subQ1}),-1.0]])]});}
            var Q6;
            {var subQ0=sQuery(id+"F5.wireOp",EDGE,"E37");var subQ1=sQuery(id+"F5.wireOp",EDGE,"E16");var subQ2=makeQuery(id+"F5.imprint","INTERSECT",VERTEX,{"disambiguationData":[OD(0.0)],"derivedFrom":[subQ1,subQ0]});Q6=makeQuery(id+"F5.imprint","IMPRINT",FACE,{"disambiguationData":[TD([[makeQuery(id+"F5.imprint","IMPRINT",EDGE,{"disambiguationData":[TD([[subQ2,-1.0]])],"derivedFrom":subQ1}),1.0]])]});}
            var Q7;
            {var subQ0=sQuery(id+"F5.wireOp",EDGE,"E37");var subQ1=sQuery(id+"F5.wireOp",EDGE,"E16");var subQ2=makeQuery(id+"F5.imprint","INTERSECT",VERTEX,{"disambiguationData":[OD(0.0)],"derivedFrom":[subQ1,subQ0]});Q7=makeQuery(id+"F5.imprint","IMPRINT",FACE,{"disambiguationData":[TD([[makeQuery(id+"F5.imprint","IMPRINT",EDGE,{"disambiguationData":[TD([[subQ2,-1.0]])],"derivedFrom":subQ1}),-1.0]])]});}
            var Q8;
            {var subQ1=sQuery(id+"F5.wireOp",EDGE,"E39.bottom");Q8=makeQuery(id+"F5.imprint","IMPRINT",FACE,{"disambiguationData":[TD([[makeQuery(id+"F5.imprint","IMPRINT",EDGE,{"derivedFrom":subQ1}),-1.0]])]});}
            var Q9;
            {var subQ0=sQuery(id+"F5.wireOp",EDGE,"E39.top");var subQ1=sQuery(id+"F5.wireOp",EDGE,"E16");var subQ2=makeQuery(id+"F5.imprint","INTERSECT",VERTEX,{"derivedFrom":[subQ1,subQ0]});Q9=makeQuery(id+"F5.imprint","IMPRINT",FACE,{"disambiguationData":[TD([[makeQuery(id+"F5.imprint","IMPRINT",EDGE,{"disambiguationData":[TD([[subQ2,-1.0]])],"derivedFrom":subQ1}),1.0]])]});}
            var Q10;
            {var subQ0=sQuery(id+"F5.wireOp",EDGE,"E38");var subQ1=sQuery(id+"F5.wireOp",EDGE,"E16");var subQ2=makeQuery(id+"F5.imprint","INTERSECT",VERTEX,{"disambiguationData":[OD(0.0)],"derivedFrom":[subQ1,subQ0]});Q10=makeQuery(id+"F5.imprint","IMPRINT",FACE,{"disambiguationData":[TD([[makeQuery(id+"F5.imprint","IMPRINT",EDGE,{"disambiguationData":[TD([[subQ2,-1.0]])],"derivedFrom":subQ1}),-1.0]])]});}
            var Q11;
            {var subQ0=sQuery(id+"F5.wireOp",EDGE,"E38");var subQ1=sQuery(id+"F5.wireOp",EDGE,"E16");var subQ2=makeQuery(id+"F5.imprint","INTERSECT",VERTEX,{"disambiguationData":[OD(0.0)],"derivedFrom":[subQ1,subQ0]});Q11=makeQuery(id+"F5.imprint","IMPRINT",FACE,{"disambiguationData":[TD([[makeQuery(id+"F5.imprint","IMPRINT",EDGE,{"disambiguationData":[TD([[subQ2,-1.0]])],"derivedFrom":subQ1}),1.0]])]});}
            extrude(context, id + "F9", {"entities" : qUnion([Q0, Q1, Q2, Q3, Q4, Q5, Q6, Q7, Q8, Q9, Q10, Q11]), "operationType" : NewBodyOperationType.ADD, "depth" : 7.7 * mm, "offsetDistance" : 25 * mm});
        }
        {
            var Q0;
            Q0=makeQuery(id+"F9.opExtrude","CAP_EDGE",EDGE,{"disambiguationData":[OSD([sQuery(id+"F5.wireOp",EDGE,"E38")])],"isStart":false});
            var Q1;
            Q1=makeQuery(id+"F9.opExtrude","CAP_FACE",FACE,{"disambiguationData":[OSD([sQuery(id+"F5.wireOp",EDGE,"E34")])],"isStart":false});
            var Q2;
            Q2=makeQuery(id+"F9.opExtrude","CAP_FACE",FACE,{"disambiguationData":[OSD([sQuery(id+"F5.wireOp",EDGE,"E35")])],"isStart":false});
            var Q3;
            Q3=makeQuery(id+"F9.opExtrude","CAP_FACE",FACE,{"disambiguationData":[OSD([sQuery(id+"F5.wireOp",EDGE,"E36")])],"isStart":false});
            var Q4;
            Q4=makeQuery(id+"F9.opExtrude","CAP_FACE",FACE,{"disambiguationData":[OSD([sQuery(id+"F5.wireOp",EDGE,"E37")])],"isStart":false});
            var Q5;
            Q5=makeQuery(id+"F9.opExtrude","CAP_EDGE",EDGE,{"disambiguationData":[OSD([sQuery(id+"F5.wireOp",EDGE,"E39.left")])],"isStart":false});
            var Q6;
            Q6=makeQuery(id+"F9.opExtrude","CAP_EDGE",EDGE,{"disambiguationData":[OSD([sQuery(id+"F5.wireOp",EDGE,"E39.right")])],"isStart":false});
            var Q7;
            Q7=makeQuery(id+"F9.opExtrude","CAP_EDGE",EDGE,{"disambiguationData":[OSD([sQuery(id+"F5.wireOp",EDGE,"E39.bottom")])],"isStart":false});
            var Q8;
            Q8=makeQuery(id+"F9.opExtrude","CAP_EDGE",EDGE,{"disambiguationData":[OSD([sQuery(id+"F5.wireOp",EDGE,"E39.top")])],"isStart":false});
            fillet(context, id + "F10", {"entities" : qUnion([Q0, Q1, Q2, Q3, Q4, Q5, Q6, Q7, Q8]), "radius" : .45 * mm, "tangentPropagation" : true, "allowEdgeOverflow" : false});
        }
        {
            var Q0;
            {var subQ0=sQuery(id+"F5.wireOp",EDGE,"E38");var subQ1=sQuery(id+"F5.wireOp",EDGE,"E16");var subQ2=makeQuery(id+"F5.imprint","INTERSECT",VERTEX,{"disambiguationData":[OD(0.0)],"derivedFrom":[subQ1,subQ0]});Q0=makeQuery(id+"F5.imprint","IMPRINT",FACE,{"disambiguationData":[TD([[makeQuery(id+"F5.imprint","IMPRINT",EDGE,{"disambiguationData":[TD([[subQ2,-1.0]])],"derivedFrom":subQ1}),-1.0]])]});}
            var Q1;
            {var subQ0=sQuery(id+"F5.wireOp",EDGE,"E38");var subQ1=sQuery(id+"F5.wireOp",EDGE,"E16");var subQ2=makeQuery(id+"F5.imprint","INTERSECT",VERTEX,{"disambiguationData":[OD(0.0)],"derivedFrom":[subQ1,subQ0]});Q1=makeQuery(id+"F5.imprint","IMPRINT",FACE,{"disambiguationData":[TD([[makeQuery(id+"F5.imprint","IMPRINT",EDGE,{"disambiguationData":[TD([[subQ2,-1.0]])],"derivedFrom":subQ1}),1.0]])]});}
            var Q2;
            {var subQ1=sQuery(id+"F5.wireOp",EDGE,"E39.bottom");Q2=makeQuery(id+"F5.imprint","IMPRINT",FACE,{"disambiguationData":[TD([[makeQuery(id+"F5.imprint","IMPRINT",EDGE,{"derivedFrom":subQ1}),-1.0]])]});}
            var Q3;
            {var subQ0=sQuery(id+"F5.wireOp",EDGE,"E39.top");var subQ1=sQuery(id+"F5.wireOp",EDGE,"E16");var subQ2=makeQuery(id+"F5.imprint","INTERSECT",VERTEX,{"derivedFrom":[subQ1,subQ0]});Q3=makeQuery(id+"F5.imprint","IMPRINT",FACE,{"disambiguationData":[TD([[makeQuery(id+"F5.imprint","IMPRINT",EDGE,{"disambiguationData":[TD([[subQ2,-1.0]])],"derivedFrom":subQ1}),1.0]])]});}
            var Q4;
            {var subQ0=sQuery(id+"F5.wireOp",EDGE,"E37");var subQ1=sQuery(id+"F5.wireOp",EDGE,"E16");var subQ2=makeQuery(id+"F5.imprint","INTERSECT",VERTEX,{"disambiguationData":[OD(0.0)],"derivedFrom":[subQ1,subQ0]});Q4=makeQuery(id+"F5.imprint","IMPRINT",FACE,{"disambiguationData":[TD([[makeQuery(id+"F5.imprint","IMPRINT",EDGE,{"disambiguationData":[TD([[subQ2,-1.0]])],"derivedFrom":subQ1}),1.0]])]});}
            var Q5;
            {var subQ0=sQuery(id+"F5.wireOp",EDGE,"E37");var subQ1=sQuery(id+"F5.wireOp",EDGE,"E16");var subQ2=makeQuery(id+"F5.imprint","INTERSECT",VERTEX,{"disambiguationData":[OD(0.0)],"derivedFrom":[subQ1,subQ0]});Q5=makeQuery(id+"F5.imprint","IMPRINT",FACE,{"disambiguationData":[TD([[makeQuery(id+"F5.imprint","IMPRINT",EDGE,{"disambiguationData":[TD([[subQ2,-1.0]])],"derivedFrom":subQ1}),-1.0]])]});}
            var Q6;
            {var subQ0=sQuery(id+"F5.wireOp",EDGE,"E36");var subQ1=sQuery(id+"F5.wireOp",EDGE,"E16");var subQ2=makeQuery(id+"F5.imprint","INTERSECT",VERTEX,{"disambiguationData":[OD(0.0)],"derivedFrom":[subQ1,subQ0]});Q6=makeQuery(id+"F5.imprint","IMPRINT",FACE,{"disambiguationData":[TD([[makeQuery(id+"F5.imprint","IMPRINT",EDGE,{"disambiguationData":[TD([[subQ2,-1.0]])],"derivedFrom":subQ1}),1.0]])]});}
            var Q7;
            {var subQ0=sQuery(id+"F5.wireOp",EDGE,"E36");var subQ1=sQuery(id+"F5.wireOp",EDGE,"E16");var subQ2=makeQuery(id+"F5.imprint","INTERSECT",VERTEX,{"disambiguationData":[OD(0.0)],"derivedFrom":[subQ1,subQ0]});Q7=makeQuery(id+"F5.imprint","IMPRINT",FACE,{"disambiguationData":[TD([[makeQuery(id+"F5.imprint","IMPRINT",EDGE,{"disambiguationData":[TD([[subQ2,-1.0]])],"derivedFrom":subQ1}),-1.0]])]});}
            var Q8;
            {var subQ0=sQuery(id+"F5.wireOp",EDGE,"E35");var subQ1=sQuery(id+"F5.wireOp",EDGE,"E16");var subQ2=makeQuery(id+"F5.imprint","INTERSECT",VERTEX,{"disambiguationData":[OD(0.0)],"derivedFrom":[subQ1,subQ0]});Q8=makeQuery(id+"F5.imprint","IMPRINT",FACE,{"disambiguationData":[TD([[makeQuery(id+"F5.imprint","IMPRINT",EDGE,{"disambiguationData":[TD([[subQ2,-1.0]])],"derivedFrom":subQ1}),1.0]])]});}
            var Q9;
            {var subQ0=sQuery(id+"F5.wireOp",EDGE,"E35");var subQ1=sQuery(id+"F5.wireOp",EDGE,"E16");var subQ2=makeQuery(id+"F5.imprint","INTERSECT",VERTEX,{"disambiguationData":[OD(0.0)],"derivedFrom":[subQ1,subQ0]});Q9=makeQuery(id+"F5.imprint","IMPRINT",FACE,{"disambiguationData":[TD([[makeQuery(id+"F5.imprint","IMPRINT",EDGE,{"disambiguationData":[TD([[subQ2,-1.0]])],"derivedFrom":subQ1}),-1.0]])]});}
            var Q10;
            {var subQ0=sQuery(id+"F5.wireOp",EDGE,"E34");var subQ1=sQuery(id+"F5.wireOp",EDGE,"E16");var subQ2=makeQuery(id+"F5.imprint","INTERSECT",VERTEX,{"disambiguationData":[OD(0.0)],"derivedFrom":[subQ1,subQ0]});Q10=makeQuery(id+"F5.imprint","IMPRINT",FACE,{"disambiguationData":[TD([[makeQuery(id+"F5.imprint","IMPRINT",EDGE,{"disambiguationData":[TD([[subQ2,-1.0]])],"derivedFrom":subQ1}),-1.0]])]});}
            var Q11;
            {var subQ0=sQuery(id+"F5.wireOp",EDGE,"E34");var subQ1=sQuery(id+"F5.wireOp",EDGE,"E16");var subQ2=makeQuery(id+"F5.imprint","INTERSECT",VERTEX,{"disambiguationData":[OD(0.0)],"derivedFrom":[subQ1,subQ0]});Q11=makeQuery(id+"F5.imprint","IMPRINT",FACE,{"disambiguationData":[TD([[makeQuery(id+"F5.imprint","IMPRINT",EDGE,{"disambiguationData":[TD([[subQ2,-1.0]])],"derivedFrom":subQ1}),1.0]])]});}
            extrude(context, id + "F11", {"entities" : qUnion([Q0, Q1, Q2, Q3, Q4, Q5, Q6, Q7, Q8, Q9, Q10, Q11]), "operationType" : NewBodyOperationType.REMOVE, "depth" : 1.8 * mm, "offsetDistance" : 25 * mm});
        }
        {
            var Q0;
            Q0=qCreatedBy(makeId("Top.planeOp"),FACE);
            var sketch = newSketch(context, id + "F12", { "sketchPlane" : qUnion([Q0])});
            skCircle(sketch, "E40", {"center": v(0, 0) * mm, "radius": 13.47 * mm});
            skSolve(sketch);
        }
        {
            var Q0;
            Q0=makeQuery(id+"F12.imprint","IMPRINT",FACE,{"disambiguationData":[TD([[makeQuery(id+"F12.imprint","IMPRINT",EDGE,{"derivedFrom":sQuery(id+"F12.wireOp",EDGE,"E40")}),1.0]])]});
            extrude(context, id + "F13", {"entities" : qUnion([Q0]), "operationType" : NewBodyOperationType.REMOVE, "depth" : 1 * mm, "offsetDistance" : 25 * mm});
        }
        {
            var Q0;
            {var subQ0=sQuery(id+"F0.wireOp",EDGE,"E7.bottom");var subQ1=sQuery(id+"F0.wireOp",EDGE,"E1.0");var subQ2=makeQuery(id+"F0.imprint","INTERSECT",VERTEX,{"disambiguationData":[OD(1.0)],"derivedFrom":[subQ1,subQ0]});Q0=makeQuery(id+"F0.imprint","IMPRINT",FACE,{"disambiguationData":[TD([[makeQuery(id+"F0.imprint","IMPRINT",EDGE,{"disambiguationData":[TD([[subQ2,-1.0]])],"derivedFrom":subQ1}),1.0]])]});}
            var Q1;
            {var subQ0=sQuery(id+"F0.wireOp",EDGE,"E3.right");var subQ1=sQuery(id+"F0.wireOp",EDGE,"E1.0");var subQ2=makeQuery(id+"F0.imprint","INTERSECT",VERTEX,{"disambiguationData":[OD(0.0)],"derivedFrom":[subQ1,subQ0]});Q1=makeQuery(id+"F0.imprint","IMPRINT",FACE,{"disambiguationData":[TD([[makeQuery(id+"F0.imprint","IMPRINT",EDGE,{"disambiguationData":[TD([[subQ2,1.0]])],"derivedFrom":subQ1}),1.0]])]});}
            var Q2;
            {var subQ0=sQuery(id+"F0.wireOp",EDGE,"E3.left");var subQ1=sQuery(id+"F0.wireOp",EDGE,"E1.0");var subQ2=makeQuery(id+"F0.imprint","INTERSECT",VERTEX,{"disambiguationData":[OD(0.0)],"derivedFrom":[subQ1,subQ0]});Q2=makeQuery(id+"F0.imprint","IMPRINT",FACE,{"disambiguationData":[TD([[makeQuery(id+"F0.imprint","IMPRINT",EDGE,{"disambiguationData":[TD([[subQ2,-1.0]])],"derivedFrom":subQ1}),1.0]])]});}
            var Q3;
            {var subQ0=sQuery(id+"F0.wireOp",EDGE,"E8.left");var subQ1=sQuery(id+"F0.wireOp",EDGE,"E1.0");var subQ2=makeQuery(id+"F0.imprint","INTERSECT",VERTEX,{"disambiguationData":[OD(0.0)],"derivedFrom":[subQ1,subQ0]});Q3=makeQuery(id+"F0.imprint","IMPRINT",FACE,{"disambiguationData":[TD([[makeQuery(id+"F0.imprint","IMPRINT",EDGE,{"disambiguationData":[TD([[subQ2,-1.0]])],"derivedFrom":subQ1}),1.0]])]});}
            var Q4;
            {var subQ0=sQuery(id+"F0.wireOp",EDGE,"E9.left");var subQ1=sQuery(id+"F0.wireOp",EDGE,"E1.0");var subQ2=makeQuery(id+"F0.imprint","INTERSECT",VERTEX,{"disambiguationData":[OD(0.0)],"derivedFrom":[subQ1,subQ0]});Q4=makeQuery(id+"F0.imprint","IMPRINT",FACE,{"disambiguationData":[TD([[makeQuery(id+"F0.imprint","IMPRINT",EDGE,{"disambiguationData":[TD([[subQ2,-1.0]])],"derivedFrom":subQ1}),1.0]])]});}
            var Q5;
            {var subQ0=sQuery(id+"F0.wireOp",EDGE,"E6.top");var subQ1=sQuery(id+"F0.wireOp",EDGE,"E1.0");var subQ2=makeQuery(id+"F0.imprint","INTERSECT",VERTEX,{"disambiguationData":[OD(0.0)],"derivedFrom":[subQ1,subQ0]});Q5=makeQuery(id+"F0.imprint","IMPRINT",FACE,{"disambiguationData":[TD([[makeQuery(id+"F0.imprint","IMPRINT",EDGE,{"disambiguationData":[TD([[subQ2,-1.0]])],"derivedFrom":subQ1}),1.0]])]});}
            var Q6;
            {var subQ0=sQuery(id+"F0.wireOp",EDGE,"E3.right");var subQ1=sQuery(id+"F0.wireOp",EDGE,"E1.0");var subQ2=makeQuery(id+"F0.imprint","INTERSECT",VERTEX,{"disambiguationData":[OD(1.0)],"derivedFrom":[subQ1,subQ0]});Q6=makeQuery(id+"F0.imprint","IMPRINT",FACE,{"disambiguationData":[TD([[makeQuery(id+"F0.imprint","IMPRINT",EDGE,{"disambiguationData":[TD([[subQ2,-1.0]])],"derivedFrom":subQ1}),1.0]])]});}
            extrude(context, id + "F14", {"entities" : qUnion([Q0, Q1, Q2, Q3, Q4, Q5, Q6]), "operationType" : NewBodyOperationType.REMOVE, "depth" : 1 * mm, "offsetDistance" : 25 * mm});
        }
        {
            var Q0;
            Q0=makeQuery(id+"F14.boolean.opBoolean","COPY",EDGE,{"derivedFrom":makeQuery(id+"F14.opExtrude","SWEPT_EDGE",EDGE,{"disambiguationData":[OSD([sQuery(id+"F0.wireOp",EDGE,"E1.0"),sQuery(id+"F0.wireOp",EDGE,"E8.left")])]})});
            var Q1;
            {var subQ0=sQuery(id+"F0.wireOp",EDGE,"E3.right");var subQ1=sQuery(id+"F0.wireOp",EDGE,"E1.0");Q1=makeQuery(id+"F14.boolean.opBoolean","COPY",EDGE,{"derivedFrom":makeQuery(id+"F14.opExtrude","SWEPT_EDGE",EDGE,{"disambiguationData":[OSD([subQ1,subQ0]),TDD([makeQuery(id+"F0.imprint","INTERSECT",VERTEX,{"disambiguationData":[OD(0.0)],"derivedFrom":[subQ1,subQ0]})])]})});}
            var Q2;
            {var subQ0=sQuery(id+"F0.wireOp",EDGE,"E6.top");var subQ1=sQuery(id+"F0.wireOp",EDGE,"E1.0");Q2=makeQuery(id+"F14.boolean.opBoolean","COPY",EDGE,{"derivedFrom":makeQuery(id+"F14.opExtrude","SWEPT_EDGE",EDGE,{"disambiguationData":[OSD([subQ1,subQ0]),TDD([makeQuery(id+"F0.imprint","INTERSECT",VERTEX,{"disambiguationData":[OD(1.0)],"derivedFrom":[subQ1,subQ0]})])]})});}
            var Q3;
            Q3=makeQuery(id+"F14.boolean.opBoolean","COPY",EDGE,{"derivedFrom":makeQuery(id+"F14.opExtrude","SWEPT_EDGE",EDGE,{"disambiguationData":[OSD([sQuery(id+"F0.wireOp",EDGE,"E1.0"),sQuery(id+"F0.wireOp",EDGE,"E9.left")])]})});
            var Q4;
            Q4=makeQuery(id+"F14.boolean.opBoolean","COPY",EDGE,{"derivedFrom":makeQuery(id+"F14.opExtrude","SWEPT_EDGE",EDGE,{"disambiguationData":[OSD([sQuery(id+"F0.wireOp",EDGE,"E1.0"),sQuery(id+"F0.wireOp",EDGE,"E2.right")])]})});
            var Q5;
            Q5=makeQuery(id+"F14.boolean.opBoolean","COPY",EDGE,{"derivedFrom":makeQuery(id+"F14.opExtrude","SWEPT_EDGE",EDGE,{"disambiguationData":[OSD([sQuery(id+"F0.wireOp",EDGE,"E1.0"),sQuery(id+"F0.wireOp",EDGE,"E6.bottom")])]})});
            var Q6;
            {var subQ0=sQuery(id+"F0.wireOp",EDGE,"E7.bottom");var subQ1=sQuery(id+"F0.wireOp",EDGE,"E1.0");Q6=makeQuery(id+"F14.boolean.opBoolean","COPY",EDGE,{"derivedFrom":makeQuery(id+"F14.opExtrude","SWEPT_EDGE",EDGE,{"disambiguationData":[OSD([subQ1,subQ0]),TDD([makeQuery(id+"F0.imprint","INTERSECT",VERTEX,{"disambiguationData":[OD(1.0)],"derivedFrom":[subQ1,subQ0]})])]})});}
            var Q7;
            {var subQ0=sQuery(id+"F0.wireOp",EDGE,"E3.left");var subQ1=sQuery(id+"F0.wireOp",EDGE,"E1.0");Q7=makeQuery(id+"F14.boolean.opBoolean","COPY",EDGE,{"derivedFrom":makeQuery(id+"F14.opExtrude","SWEPT_EDGE",EDGE,{"disambiguationData":[OSD([subQ1,subQ0]),TDD([makeQuery(id+"F0.imprint","INTERSECT",VERTEX,{"disambiguationData":[OD(0.0)],"derivedFrom":[subQ1,subQ0]})])]})});}
            var Q8;
            {var subQ0=sQuery(id+"F0.wireOp",EDGE,"E7.bottom");var subQ1=sQuery(id+"F0.wireOp",EDGE,"E1.0");Q8=makeQuery(id+"F14.boolean.opBoolean","COPY",EDGE,{"derivedFrom":makeQuery(id+"F14.opExtrude","SWEPT_EDGE",EDGE,{"disambiguationData":[OSD([subQ1,subQ0]),TDD([makeQuery(id+"F0.imprint","INTERSECT",VERTEX,{"disambiguationData":[OD(0.0)],"derivedFrom":[subQ1,subQ0]})])]})});}
            var Q9;
            Q9=makeQuery(id+"F14.boolean.opBoolean","COPY",EDGE,{"derivedFrom":makeQuery(id+"F14.opExtrude","SWEPT_EDGE",EDGE,{"disambiguationData":[OSD([sQuery(id+"F0.wireOp",EDGE,"E1.0"),sQuery(id+"F0.wireOp",EDGE,"E9.right")])]})});
            var Q10;
            {var subQ0=sQuery(id+"F0.wireOp",EDGE,"E6.top");var subQ1=sQuery(id+"F0.wireOp",EDGE,"E1.0");Q10=makeQuery(id+"F14.boolean.opBoolean","COPY",EDGE,{"derivedFrom":makeQuery(id+"F14.opExtrude","SWEPT_EDGE",EDGE,{"disambiguationData":[OSD([subQ1,subQ0]),TDD([makeQuery(id+"F0.imprint","INTERSECT",VERTEX,{"disambiguationData":[OD(0.0)],"derivedFrom":[subQ1,subQ0]})])]})});}
            var Q11;
            {var subQ0=sQuery(id+"F0.wireOp",EDGE,"E3.right");var subQ1=sQuery(id+"F0.wireOp",EDGE,"E1.0");Q11=makeQuery(id+"F14.boolean.opBoolean","COPY",EDGE,{"derivedFrom":makeQuery(id+"F14.opExtrude","SWEPT_EDGE",EDGE,{"disambiguationData":[OSD([subQ1,subQ0]),TDD([makeQuery(id+"F0.imprint","INTERSECT",VERTEX,{"disambiguationData":[OD(1.0)],"derivedFrom":[subQ1,subQ0]})])]})});}
            var Q12;
            {var subQ0=sQuery(id+"F0.wireOp",EDGE,"E3.left");var subQ1=sQuery(id+"F0.wireOp",EDGE,"E1.0");Q12=makeQuery(id+"F14.boolean.opBoolean","COPY",EDGE,{"derivedFrom":makeQuery(id+"F14.opExtrude","SWEPT_EDGE",EDGE,{"disambiguationData":[OSD([subQ1,subQ0]),TDD([makeQuery(id+"F0.imprint","INTERSECT",VERTEX,{"disambiguationData":[OD(1.0)],"derivedFrom":[subQ1,subQ0]})])]})});}
            var Q13;
            Q13=makeQuery(id+"F14.boolean.opBoolean","COPY",EDGE,{"derivedFrom":makeQuery(id+"F14.opExtrude","SWEPT_EDGE",EDGE,{"disambiguationData":[OSD([sQuery(id+"F0.wireOp",EDGE,"E1.0"),sQuery(id+"F0.wireOp",EDGE,"E2.left")])]})});
            fillet(context, id + "F15", {"entities" : qUnion([Q0, Q1, Q2, Q3, Q4, Q5, Q6, Q7, Q8, Q9, Q10, Q11, Q12, Q13]), "radius" : 1 * mm, "tangentPropagation" : true, "allowEdgeOverflow" : false});
        }
        {
            var Q0;
            {var subQ0=sQuery(id+"F0.wireOp",EDGE,"E12");Q0=makeQuery(id+"F0.imprint","IMPRINT",FACE,{"disambiguationData":[TD([[makeQuery(id+"F0.imprint","IMPRINT",EDGE,{"derivedFrom":subQ0}),-1.0]])]});}
            var Q1;
            {var subQ0=sQuery(id+"F0.wireOp",EDGE,"E11");var subQ5=sQuery(id+"F0.wireOp",EDGE,"E8.left");var subQ6=makeQuery(id+"F0.imprint","INTERSECT",VERTEX,{"disambiguationData":[OD(1.0)],"derivedFrom":[subQ5,subQ0]});Q1=makeQuery(id+"F0.imprint","IMPRINT",FACE,{"disambiguationData":[TD([[makeQuery(id+"F0.imprint","IMPRINT",EDGE,{"disambiguationData":[TD([[subQ6,-1.0]])],"derivedFrom":subQ5}),-1.0]])]});}
            var Q2;
            {var subQ0=sQuery(id+"F0.wireOp",EDGE,"E11");var subQ1=sQuery(id+"F0.wireOp",EDGE,"E8.left");var subQ2=makeQuery(id+"F0.imprint","INTERSECT",VERTEX,{"disambiguationData":[OD(1.0)],"derivedFrom":[subQ1,subQ0]});Q2=makeQuery(id+"F0.imprint","IMPRINT",FACE,{"disambiguationData":[TD([[makeQuery(id+"F0.imprint","IMPRINT",EDGE,{"disambiguationData":[TD([[subQ2,-1.0]])],"derivedFrom":subQ1}),1.0]])]});}
            var Q3;
            {var subQ0=sQuery(id+"F0.wireOp",EDGE,"E11");var subQ1=sQuery(id+"F0.wireOp",EDGE,"E8.right");var subQ2=makeQuery(id+"F0.imprint","INTERSECT",VERTEX,{"disambiguationData":[OD(1.0)],"derivedFrom":[subQ1,subQ0]});Q3=makeQuery(id+"F0.imprint","IMPRINT",FACE,{"disambiguationData":[TD([[makeQuery(id+"F0.imprint","IMPRINT",EDGE,{"disambiguationData":[TD([[subQ2,-1.0]])],"derivedFrom":subQ1}),1.0]])]});}
            var Q4;
            {var subQ0=sQuery(id+"F0.wireOp",EDGE,"E11");var subQ1=sQuery(id+"F0.wireOp",EDGE,"E9.left");var subQ2=makeQuery(id+"F0.imprint","INTERSECT",VERTEX,{"disambiguationData":[OD(1.0)],"derivedFrom":[subQ1,subQ0]});Q4=makeQuery(id+"F0.imprint","IMPRINT",FACE,{"disambiguationData":[TD([[makeQuery(id+"F0.imprint","IMPRINT",EDGE,{"disambiguationData":[TD([[subQ2,-1.0]])],"derivedFrom":subQ1}),1.0]])]});}
            var Q5;
            {var subQ0=sQuery(id+"F0.wireOp",EDGE,"E11");var subQ5=sQuery(id+"F0.wireOp",EDGE,"E9.right");var subQ6=makeQuery(id+"F0.imprint","INTERSECT",VERTEX,{"disambiguationData":[OD(1.0)],"derivedFrom":[subQ5,subQ0]});Q5=makeQuery(id+"F0.imprint","IMPRINT",FACE,{"disambiguationData":[TD([[makeQuery(id+"F0.imprint","IMPRINT",EDGE,{"disambiguationData":[TD([[subQ6,-1.0]])],"derivedFrom":subQ5}),1.0]])]});}
            var Q6;
            {var subQ0=sQuery(id+"F0.wireOp",EDGE,"E13");Q6=makeQuery(id+"F0.imprint","IMPRINT",FACE,{"disambiguationData":[TD([[makeQuery(id+"F0.imprint","IMPRINT",EDGE,{"derivedFrom":subQ0}),-1.0]])]});}
            extrude(context, id + "F16", {"entities" : qUnion([Q0, Q1, Q2, Q3, Q4, Q5, Q6]), "operationType" : NewBodyOperationType.ADD, "depth" : 1 * mm, "offsetDistance" : 25 * mm});
        }
    });
